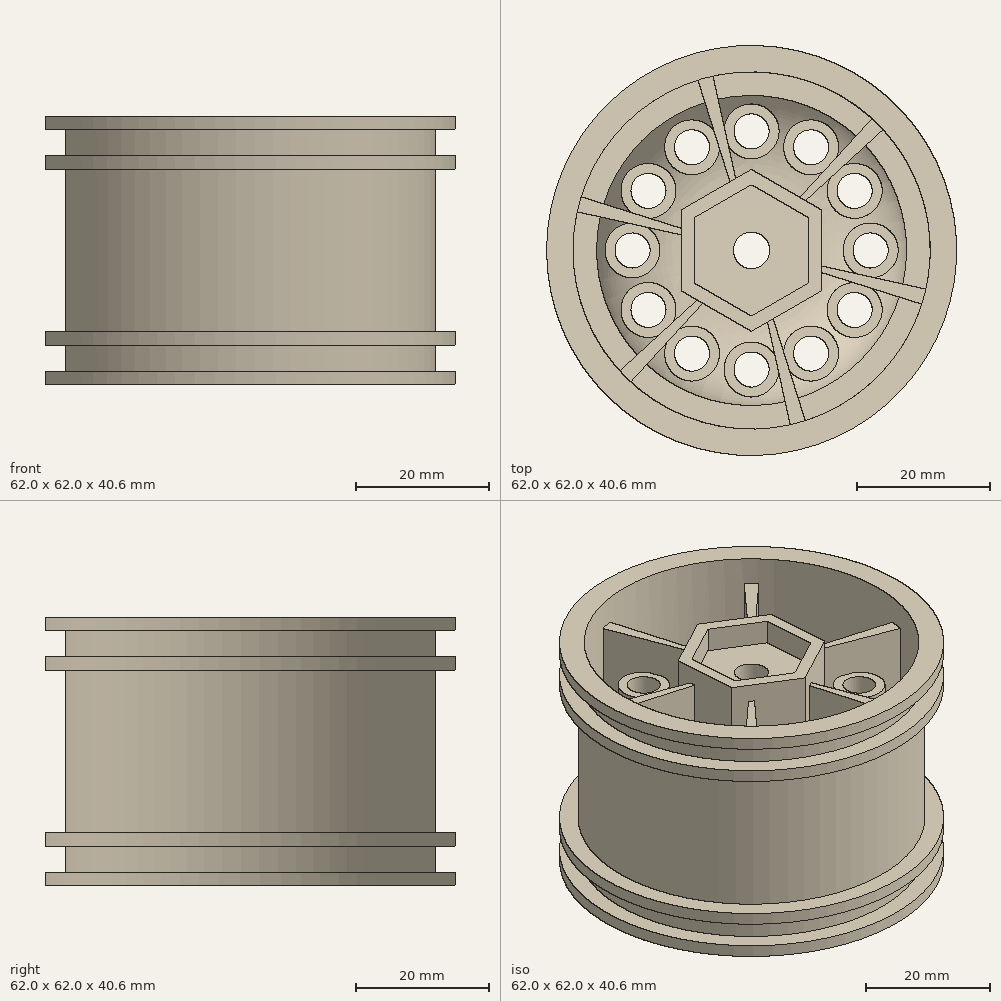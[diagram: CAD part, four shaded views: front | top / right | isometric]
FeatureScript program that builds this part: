
annotation { "Feature Type Name" : "Feature", "Feature Type Description" : "" }
export const myFeature = defineFeature(function(context is Context, id is Id, definition is map)
    precondition{}
    {
        {
            var Q0;
            Q0=qCreatedBy(makeId("Front.planeOp"),FACE);
            var sketch = newSketch(context, id + "F0", { "sketchPlane" : qUnion([Q0])});
            skLineSegment(sketch, "E0", {"start": v(31, 40.6) * mm, "end": v(0, 40.6) * mm, "construction": true});
            skLineSegment(sketch, "E1", {"start": v(0, 0) * mm, "end": v(0, 40.6) * mm});
            skPoint(sketch, "E2", {"position": v(0, 20.3) * mm});
            skLineSegment(sketch, "E3", {"start": v(31, 0) * mm, "end": v(31, 2) * mm});
            skLineSegment(sketch, "E4", {"start": v(31, 2) * mm, "end": v(28, 2) * mm});
            skLineSegment(sketch, "E5", {"start": v(28, 2) * mm, "end": v(28, 6) * mm});
            skLineSegment(sketch, "E6", {"start": v(28, 6) * mm, "end": v(31, 6) * mm});
            skLineSegment(sketch, "E7", {"start": v(31, 6) * mm, "end": v(31, 8) * mm});
            skLineSegment(sketch, "E8", {"start": v(31, 8) * mm, "end": v(28, 8) * mm});
            skLineSegment(sketch, "E9", {"start": v(28, 8) * mm, "end": v(28, 20.3) * mm});
            skLineSegment(sketch, "E10", {"start": v(31, 0) * mm, "end": v(27, 0) * mm});
            skLineSegment(sketch, "E11", {"start": v(0, 20.3) * mm, "end": v(28, 20.3) * mm, "construction": true});
            skLineSegment(sketch, "E12.MirrorCS", {"start": v(28, 32.6) * mm, "end": v(28, 20.3) * mm});
            skLineSegment(sketch, "E13.MirrorCS", {"start": v(31, 32.6) * mm, "end": v(28, 32.6) * mm});
            skLineSegment(sketch, "E14.MirrorCS", {"start": v(31, 34.6) * mm, "end": v(31, 32.6) * mm});
            skLineSegment(sketch, "E15.MirrorCS", {"start": v(28, 34.6) * mm, "end": v(31, 34.6) * mm});
            skLineSegment(sketch, "E16.MirrorCS", {"start": v(28, 38.6) * mm, "end": v(28, 34.6) * mm});
            skLineSegment(sketch, "E17.MirrorCS", {"start": v(31, 38.6) * mm, "end": v(28, 38.6) * mm});
            skLineSegment(sketch, "E18.MirrorCS", {"start": v(31, 40.6) * mm, "end": v(31, 38.6) * mm});
            skLineSegment(sketch, "E19", {"start": v(0, 20.3) * mm, "end": v(0, 24) * mm});
            skLineSegment(sketch, "E20.MirrorCS", {"start": v(31, 40.6) * mm, "end": v(27, 40.6) * mm});
            skLineSegment(sketch, "E21", {"start": v(27, 0) * mm, "end": v(27, 12) * mm});
            skLineSegment(sketch, "E22", {"start": v(27, 12) * mm, "end": v(22.5, 12) * mm});
            skLineSegment(sketch, "E23", {"start": v(0, 20.3) * mm, "end": v(10, 20.3) * mm});
            skArc(sketch, "E24", {"start": v(22.5, 12) * mm, "mid": v(18.66, 20.51) * mm, "end": v(10, 24) * mm});
            skLineSegment(sketch, "E25", {"start": v(10, 24) * mm, "end": v(0, 24) * mm});
            skLineSegment(sketch, "E26.0", {"start": v(10, 25) * mm, "end": v(0, 25) * mm});
            skArc(sketch, "E26.1", {"start": v(23.43, 13) * mm, "mid": v(19, 21.56) * mm, "end": v(10, 25) * mm});
            skLineSegment(sketch, "E26.2", {"start": v(27, 13) * mm, "end": v(23.43, 13) * mm});
            skLineSegment(sketch, "E27", {"start": v(27, 40.6) * mm, "end": v(27, 13) * mm});
            skSolve(sketch);
        }
        {
            var Q0;
            Q0=makeQuery(id+"F0.imprint","IMPRINT",FACE,{"disambiguationData":[TD([[makeQuery(id+"F0.imprint","IMPRINT",EDGE,{"derivedFrom":sQuery(id+"F0.wireOp",EDGE,"E3")}),1.0]])]});
            var Q1;
            Q1=sQuery(id+"F0.wireOp",EDGE,"E1");
            revolve(context, id + "F1", {"entities" : qUnion([Q0]), "axis" : qUnion([Q1]), "revolveType" : RevolveType.FULL});
        }
        {
            var Q0;
            Q0=makeQuery(id+"F1.opRevolve","SWEPT_FACE",FACE,{"disambiguationData":[OSD([sQuery(id+"F0.wireOp",EDGE,"E26.0")])]});
            cPlane(context, id + "F2", {"entities" : qUnion([Q0]), "cplaneType" : CPlaneType.OFFSET, "offset" : 5 * mm, "width" : 150 * mm, "height" : 150 * mm});
        }
        {
            var Q0;
            Q0=qCreatedBy(id+"F2.planeOp",FACE);
            var sketch = newSketch(context, id + "F17", { "sketchPlane" : qUnion([Q0])});
            skCircle(sketch, "E28", {"center": v(18, 0) * mm, "radius": 2.65 * mm});
            skCircle(sketch, "E29.0", {"center": v(18, 0) * mm, "radius": 4.15 * mm});
            skSolve(sketch);
        }
        {
            var Q0;
            Q0=makeQuery(id+"F17.imprint","IMPRINT",FACE,{"disambiguationData":[TD([[makeQuery(id+"F17.imprint","IMPRINT",EDGE,{"derivedFrom":sQuery(id+"F17.wireOp",EDGE,"E28")}),1.0]])]});
            extrude(context, id + "F18", {"entities" : qUnion([Q0]), "endBound" : BoundingType.THROUGH_ALL, "oppositeDirection" : true, "depth" : 25 * mm});
        }
        {
            var Q0;
            Q0=makeQuery(id+"F17.imprint","IMPRINT",FACE,{"disambiguationData":[TD([[makeQuery(id+"F17.imprint","IMPRINT",EDGE,{"derivedFrom":sQuery(id+"F17.wireOp",EDGE,"E28")}),-1.0]])]});
            extrude(context, id + "F3", {"entities" : qUnion([Q0]), "endBound" : BoundingType.UP_TO_NEXT, "oppositeDirection" : true, "depth" : 25 * mm});
        }
        {
            var Q0;
            Q0=makeQuery(id+"F18.opExtrude","SWEPT_BODY",BODY,{"disambiguationData":[OSD([sQuery(id+"F17.wireOp",EDGE,"E28")])]});
            var Q1;
            Q1=sQuery(id+"F0.wireOp",EDGE,"E1");
            circularPattern(context, id + "F19", {"operationType" : NewBodyOperationType.REMOVE, "entities" : qUnion([Q0]), "axis" : qUnion([Q1]), "angle" : 360 * degree, "instanceCount" : 12, "oppositeDirection" : true, "equalSpace" : true});
        }
        {
            var Q0;
            Q0=makeQuery(id+"F3.opExtrude","SWEPT_BODY",BODY,{"disambiguationData":[OSD([sQuery(id+"F17.wireOp",EDGE,"E28"),sQuery(id+"F17.wireOp",EDGE,"E29.0")])]});
            var Q1;
            Q1=sQuery(id+"F0.wireOp",EDGE,"E1");
            circularPattern(context, id + "F4", {"operationType" : NewBodyOperationType.ADD, "entities" : qUnion([Q0]), "axis" : qUnion([Q1]), "angle" : 360 * degree, "instanceCount" : 12, "equalSpace" : true});
        }
        {
            var Q0;
            Q0=makeQuery(id+"F1.opRevolve","SWEPT_FACE",FACE,{"disambiguationData":[OSD([sQuery(id+"F0.wireOp",EDGE,"E26.0")])]});
            cPlane(context, id + "F5", {"entities" : qUnion([Q0]), "cplaneType" : CPlaneType.OFFSET, "offset" : 10 * mm, "width" : 150 * mm, "height" : 150 * mm});
        }
        {
            var Q0;
            Q0=qCreatedBy(id+"F5.planeOp",FACE);
            var sketch = newSketch(context, id + "F20", { "sketchPlane" : qUnion([Q0])});
            skCircle(sketch, "E30", {"center": v(0, 0) * mm, "radius": 2.75 * mm});
            skCircle(sketch, "E31.cCircle", {"center": v(0, 0) * mm, "radius": 8.6 * mm, "construction": true});
            skLineSegment(sketch, "E31.0", {"start": v(-8.6, 4.97) * mm, "end": v(0, 9.93) * mm});
            skLineSegment(sketch, "E31.1", {"start": v(0, 9.93) * mm, "end": v(8.6, 4.97) * mm});
            skLineSegment(sketch, "E31.2", {"start": v(8.6, 4.97) * mm, "end": v(8.6, -4.97) * mm});
            skLineSegment(sketch, "E31.3", {"start": v(8.6, -4.97) * mm, "end": v(0, -9.93) * mm});
            skLineSegment(sketch, "E31.4", {"start": v(0, -9.93) * mm, "end": v(-8.6, -4.97) * mm});
            skLineSegment(sketch, "E31.5", {"start": v(-8.6, -4.97) * mm, "end": v(-8.6, 4.97) * mm});
            skPoint(sketch, "E31.0.midPoint", {"position": v(-4.3, 7.45) * mm});
            skLineSegment(sketch, "E32.0", {"start": v(10.6, 6.12) * mm, "end": v(10.6, -6.12) * mm});
            skLineSegment(sketch, "E32.1", {"start": v(0, -12.24) * mm, "end": v(-10.6, -6.12) * mm});
            skLineSegment(sketch, "E32.2", {"start": v(-10.6, -6.12) * mm, "end": v(-10.6, 6.12) * mm});
            skLineSegment(sketch, "E32.3", {"start": v(10.6, -6.12) * mm, "end": v(0, -12.24) * mm});
            skLineSegment(sketch, "E32.4", {"start": v(-10.6, 6.12) * mm, "end": v(0, 12.24) * mm});
            skLineSegment(sketch, "E32.5", {"start": v(0, 12.24) * mm, "end": v(10.6, 6.12) * mm});
            skCircle(sketch, "E33", {"center": v(0, 0) * mm, "radius": 6 * mm});
            skSolve(sketch);
        }
        {
            var Q0;
            Q0=makeQuery(id+"F20.imprint","IMPRINT",FACE,{"disambiguationData":[TD([[makeQuery(id+"F20.imprint","IMPRINT",EDGE,{"derivedFrom":sQuery(id+"F20.wireOp",EDGE,"E31.0")}),1.0]])]});
            var Q1;
            Q1=makeQuery(id+"F20.imprint","IMPRINT",FACE,{"disambiguationData":[TD([[makeQuery(id+"F20.imprint","IMPRINT",EDGE,{"derivedFrom":sQuery(id+"F20.wireOp",EDGE,"E30")}),-1.0]])]});
            var Q2;
            Q2=makeQuery(id+"F20.imprint","IMPRINT",FACE,{"disambiguationData":[TD([[makeQuery(id+"F20.imprint","IMPRINT",EDGE,{"derivedFrom":sQuery(id+"F20.wireOp",EDGE,"E30")}),1.0]])]});
            var Q3;
            Q3=makeQuery(id+"F20.imprint","IMPRINT",FACE,{"disambiguationData":[TD([[makeQuery(id+"F20.imprint","IMPRINT",EDGE,{"derivedFrom":sQuery(id+"F20.wireOp",EDGE,"E31.0")}),-1.0]])]});
            extrude(context, id + "F6", {"entities" : qUnion([Q0, Q1, Q2, Q3]), "operationType" : NewBodyOperationType.ADD, "endBound" : BoundingType.UP_TO_NEXT, "oppositeDirection" : true, "depth" : 20 * mm});
        }
        {
            var Q0;
            Q0=makeQuery(id+"F20.imprint","IMPRINT",FACE,{"disambiguationData":[TD([[makeQuery(id+"F20.imprint","IMPRINT",EDGE,{"derivedFrom":sQuery(id+"F20.wireOp",EDGE,"E31.0")}),1.0]])]});
            extrude(context, id + "F7", {"entities" : qUnion([Q0]), "operationType" : NewBodyOperationType.ADD, "depth" : 4 * mm});
        }
        {
            var Q0;
            Q0=makeQuery(id+"F20.imprint","IMPRINT",FACE,{"disambiguationData":[TD([[makeQuery(id+"F20.imprint","IMPRINT",EDGE,{"derivedFrom":sQuery(id+"F20.wireOp",EDGE,"E30")}),-1.0]])]});
            var Q1;
            Q1=makeQuery(id+"F20.imprint","IMPRINT",FACE,{"disambiguationData":[TD([[makeQuery(id+"F20.imprint","IMPRINT",EDGE,{"derivedFrom":sQuery(id+"F20.wireOp",EDGE,"E30")}),1.0]])]});
            extrude(context, id + "F8", {"entities" : qUnion([Q0, Q1]), "operationType" : NewBodyOperationType.REMOVE, "oppositeDirection" : true, "depth" : 25 * mm});
        }
        {
            var Q0;
            Q0=makeQuery(id+"F20.imprint","IMPRINT",FACE,{"disambiguationData":[TD([[makeQuery(id+"F20.imprint","IMPRINT",EDGE,{"derivedFrom":sQuery(id+"F20.wireOp",EDGE,"E30")}),-1.0]])]});
            extrude(context, id + "F21", {"entities" : qUnion([Q0]), "operationType" : NewBodyOperationType.ADD, "oppositeDirection" : true, "depth" : 5.5 * mm});
        }
        {
            var Q0;
            Q0=makeQuery(id+"F1.opRevolve","SWEPT_FACE",FACE,{"disambiguationData":[OSD([sQuery(id+"F0.wireOp",EDGE,"E20.MirrorCS")])]});
            var sketch = newSketch(context, id + "F22", { "sketchPlane" : qUnion([Q0])});
            skCircle(sketch, "E34.0", {"center": v(9, -15.59) * mm, "radius": 4.15 * mm});
            skCircle(sketch, "E35.0", {"center": v(0, 0) * mm, "radius": 27 * mm});
            skLineSegment(sketch, "E36", {"start": v(0, 0) * mm, "end": v(6.99, -26.08) * mm});
            skLineSegment(sketch, "E37", {"start": v(5, -16.66) * mm, "end": v(4, -16.93) * mm});
            skCircle(sketch, "E38.0", {"center": v(0, -18) * mm, "radius": 4.15 * mm});
            skPoint(sketch, "E39", {"position": v(4.5, -16.8) * mm});
            skLineSegment(sketch, "E40", {"start": v(16.26, -23.6) * mm, "end": v(-9.38, -30.46) * mm});
            skSolve(sketch);
        }
        {
            var Q0;
            Q0=sQuery(id+"F22.wireOp",EDGE,"E36");
            var Q1;
            Q1=qCreatedBy(makeId("Origin.pointOp"),VERTEX);
            cPlane(context, id + "F9", {"entities" : qUnion([Q0, Q1]), "cplaneType" : CPlaneType.LINE_ANGLE, "offset" : 25 * mm, "angle" : 0 * degree, "width" : 150 * mm, "height" : 150 * mm});
        }
        {
            var Q0;
            Q0=qCreatedBy(id+"F9.planeOp",FACE);
            var sketch = newSketch(context, id + "F10", { "sketchPlane" : qUnion([Q0])});
            skLineSegment(sketch, "E41", {"start": v(31, 40.6) * mm, "end": v(0, 40.6) * mm, "construction": true});
            skLineSegment(sketch, "E42", {"start": v(0, 0) * mm, "end": v(0, 40.6) * mm});
            skPoint(sketch, "E43", {"position": v(0, 20.3) * mm});
            skLineSegment(sketch, "E44", {"start": v(31, 0) * mm, "end": v(31, 2) * mm});
            skLineSegment(sketch, "E45", {"start": v(31, 2) * mm, "end": v(28, 2) * mm});
            skLineSegment(sketch, "E46", {"start": v(28, 2) * mm, "end": v(28, 6) * mm});
            skLineSegment(sketch, "E47", {"start": v(28, 6) * mm, "end": v(31, 6) * mm});
            skLineSegment(sketch, "E48", {"start": v(31, 6) * mm, "end": v(31, 8) * mm});
            skLineSegment(sketch, "E49", {"start": v(31, 8) * mm, "end": v(28, 8) * mm});
            skLineSegment(sketch, "E50", {"start": v(28, 8) * mm, "end": v(28, 20.3) * mm});
            skLineSegment(sketch, "E51", {"start": v(31, 0) * mm, "end": v(27, 0) * mm});
            skLineSegment(sketch, "E52", {"start": v(0, 20.3) * mm, "end": v(28, 20.3) * mm, "construction": true});
            skLineSegment(sketch, "E53.MirrorCS", {"start": v(28, 32.6) * mm, "end": v(28, 20.3) * mm});
            skLineSegment(sketch, "E54.MirrorCS", {"start": v(31, 32.6) * mm, "end": v(28, 32.6) * mm});
            skLineSegment(sketch, "E55.MirrorCS", {"start": v(31, 34.6) * mm, "end": v(31, 32.6) * mm});
            skLineSegment(sketch, "E56.MirrorCS", {"start": v(28, 34.6) * mm, "end": v(31, 34.6) * mm});
            skLineSegment(sketch, "E57.MirrorCS", {"start": v(28, 38.6) * mm, "end": v(28, 34.6) * mm});
            skLineSegment(sketch, "E58.MirrorCS", {"start": v(31, 38.6) * mm, "end": v(28, 38.6) * mm});
            skLineSegment(sketch, "E59.MirrorCS", {"start": v(31, 40.6) * mm, "end": v(31, 38.6) * mm});
            skLineSegment(sketch, "E60", {"start": v(0, 20.3) * mm, "end": v(0, 24) * mm});
            skLineSegment(sketch, "E61.MirrorCS", {"start": v(31, 40.6) * mm, "end": v(27, 40.6) * mm});
            skLineSegment(sketch, "E62", {"start": v(27, 0) * mm, "end": v(27, 12) * mm});
            skLineSegment(sketch, "E63", {"start": v(27, 12) * mm, "end": v(22.5, 12) * mm});
            skLineSegment(sketch, "E64", {"start": v(0, 20.3) * mm, "end": v(10, 20.3) * mm});
            skArc(sketch, "E65", {"start": v(22.5, 12) * mm, "mid": v(18.66, 20.51) * mm, "end": v(10, 24) * mm});
            skLineSegment(sketch, "E66", {"start": v(10, 24) * mm, "end": v(0, 24) * mm});
            skLineSegment(sketch, "E67.0", {"start": v(10, 25) * mm, "end": v(0, 25) * mm});
            skArc(sketch, "E67.1", {"start": v(23.43, 13) * mm, "mid": v(19, 21.56) * mm, "end": v(10, 25) * mm});
            skLineSegment(sketch, "E67.2", {"start": v(27, 13) * mm, "end": v(23.43, 13) * mm});
            skLineSegment(sketch, "E68", {"start": v(27, 40.6) * mm, "end": v(27, 13) * mm});
            skLineSegment(sketch, "E69.0.0", {"start": v(-8.65, 39) * mm, "end": v(3.17, 39) * mm});
            skLineSegment(sketch, "E69.0.1", {"start": v(3.17, 39) * mm, "end": v(11.82, 39) * mm});
            skLineSegment(sketch, "E69.0.2", {"start": v(11.82, 39) * mm, "end": v(8.65, 39) * mm});
            skLineSegment(sketch, "E69.0.3", {"start": v(8.65, 39) * mm, "end": v(-3.17, 39) * mm});
            skLineSegment(sketch, "E69.0.4", {"start": v(-3.17, 39) * mm, "end": v(-11.82, 39) * mm});
            skLineSegment(sketch, "E69.0.5", {"start": v(-11.82, 39) * mm, "end": v(-8.65, 39) * mm});
            skLineSegment(sketch, "E70.0.0", {"start": v(3.17, 39) * mm, "end": v(3.17, 24.81) * mm});
            skFitSpline(sketch, "E70.0.1", {"points": [v(3.14, 24.83) * mm, v(3.85, 24.91) * mm, v(5.28, 24.98) * mm, v(7.42, 25) * mm, v(9.57, 24.98) * mm, v(11, 24.91) * mm, v(11.71, 24.83) * mm]});
            skLineSegment(sketch, "E70.0.2", {"start": v(11.82, 24.81) * mm, "end": v(11.82, 39) * mm});
            skLineSegment(sketch, "E70.0.3", {"start": v(11.82, 39) * mm, "end": v(3.17, 39) * mm});
            skLineSegment(sketch, "E71.0.0", {"start": v(7.02, 35) * mm, "end": v(9.6, 35) * mm});
            skLineSegment(sketch, "E71.0.1", {"start": v(9.6, 35) * mm, "end": v(9.6, 39) * mm});
            skLineSegment(sketch, "E71.0.2", {"start": v(9.6, 39) * mm, "end": v(7.02, 39) * mm});
            skLineSegment(sketch, "E71.0.3", {"start": v(7.02, 39) * mm, "end": v(7.02, 35) * mm});
            skLineSegment(sketch, "E72", {"start": v(11.82, 36) * mm, "end": v(27, 36) * mm});
            skLineSegment(sketch, "E73", {"start": v(11.82, 36) * mm, "end": v(10.82, 36) * mm});
            skLineSegment(sketch, "E74", {"start": v(10.82, 36) * mm, "end": v(10.82, 24.97) * mm});
            skSolve(sketch);
        }
        {
            var Q0;
            {var subQ5=sQuery(id+"F10.wireOp",EDGE,"E67.2");Q0=makeQuery(id+"F10.imprint","IMPRINT",FACE,{"disambiguationData":[TD([[makeQuery(id+"F10.imprint","IMPRINT",EDGE,{"derivedFrom":subQ5}),-1.0]])]});}
            var Q1;
            {var subQ4=sQuery(id+"F10.wireOp",EDGE,"E73");Q1=makeQuery(id+"F10.imprint","IMPRINT",FACE,{"disambiguationData":[TD([[makeQuery(id+"F10.imprint","IMPRINT",EDGE,{"derivedFrom":subQ4}),1.0]])]});}
            var Q2;
            Q2=sQuery(id+"F0.wireOp",EDGE,"E1");
            revolve(context, id + "F11", {"entities" : qUnion([Q0, Q1]), "axis" : qUnion([Q2]), "revolveType" : RevolveType.SYMMETRIC, "angle" : 5 * degree});
        }
        {
            var Q0;
            Q0=makeQuery(id+"F11.opRevolve","SWEPT_BODY",BODY,{"disambiguationData":[OSD([sQuery(id+"F10.wireOp",EDGE,"E67.1"),sQuery(id+"F10.wireOp",EDGE,"E67.2"),sQuery(id+"F10.wireOp",EDGE,"E68"),sQuery(id+"F10.wireOp",EDGE,"E72"),sQuery(id+"F10.wireOp",EDGE,"E73"),sQuery(id+"F10.wireOp",EDGE,"E74")])]});
            var Q1;
            Q1=sQuery(id+"F0.wireOp",EDGE,"E1");
            circularPattern(context, id + "F12", {"operationType" : NewBodyOperationType.ADD, "entities" : qUnion([Q0]), "axis" : qUnion([Q1]), "angle" : 360 * degree, "instanceCount" : 6, "equalSpace" : true});
        }
        {
            var Q0;
            Q0=makeQuery(id+"F1.opRevolve","SWEPT_FACE",FACE,{"disambiguationData":[OSD([sQuery(id+"F0.wireOp",EDGE,"E25")])]});
            var sketch = newSketch(context, id + "F13", { "sketchPlane" : qUnion([Q0])});
            skArc(sketch, "E75", {"start": v(-8, 0) * mm, "mid": v(-9, 1) * mm, "end": v(-10, 0) * mm});
            skLineSegment(sketch, "E76", {"start": v(-0.63, 0) * mm, "end": v(-14.19, 0) * mm, "construction": true});
            skLineSegment(sketch, "E77", {"start": v(-10, 0) * mm, "end": v(-8, 0) * mm});
            skSolve(sketch);
        }
        {
            var Q0;
            Q0=makeQuery(id+"F13.imprint","IMPRINT",FACE,{"disambiguationData":[TD([[makeQuery(id+"F13.imprint","IMPRINT",EDGE,{"derivedFrom":sQuery(id+"F13.wireOp",EDGE,"E75")}),1.0]])]});
            var Q1;
            Q1=sQuery(id+"F13.wireOp",EDGE,"E77");
            revolve(context, id + "F23", {"entities" : qUnion([Q0]), "axis" : qUnion([Q1]), "revolveType" : RevolveType.FULL});
        }
        {
            var Q0;
            Q0=makeQuery(id+"F23.opRevolve","SWEPT_BODY",BODY,{"disambiguationData":[OSD([sQuery(id+"F13.wireOp",EDGE,"E75"),sQuery(id+"F13.wireOp",EDGE,"E77")])]});
            var Q1;
            Q1=qCreatedBy(makeId("Origin.pointOp"),BODY);
            var Q2;
            Q2=makeQuery(id+"F8.boolean.opBoolean","INTERSECT",EDGE,{"derivedFrom":[makeQuery(id+"F1.opRevolve","SWEPT_FACE",FACE,{"disambiguationData":[OSD([sQuery(id+"F0.wireOp",EDGE,"E25")])]}),makeQuery(id+"F8.opExtrude","SWEPT_FACE",FACE,{"disambiguationData":[OSD([sQuery(id+"F20.wireOp",EDGE,"E33")])]})]});
            circularPattern(context, id + "F24", {"operationType" : NewBodyOperationType.ADD, "entities" : qUnion([Q0, Q1]), "axis" : qUnion([Q2]), "angle" : 360 * degree, "instanceCount" : 5, "equalSpace" : true});
        }
        {
            var Q0;
            Q0=makeQuery(id+"F1.opRevolve","SWEPT_FACE",FACE,{"disambiguationData":[OSD([sQuery(id+"F0.wireOp",EDGE,"E22")])]});
            var sketch = newSketch(context, id + "F14", { "sketchPlane" : qUnion([Q0])});
            skArc(sketch, "E78", {"start": v(-24, 0) * mm, "mid": v(-25, 1) * mm, "end": v(-26, 0) * mm});
            skLineSegment(sketch, "E79", {"start": v(-26, 0) * mm, "end": v(-24, 0) * mm});
            skSolve(sketch);
        }
        {
            var Q0;
            Q0=makeQuery(id+"F14.imprint","IMPRINT",FACE,{"disambiguationData":[TD([[makeQuery(id+"F14.imprint","IMPRINT",EDGE,{"derivedFrom":sQuery(id+"F14.wireOp",EDGE,"E78")}),1.0]])]});
            var Q1;
            Q1=sQuery(id+"F14.wireOp",EDGE,"E79");
            revolve(context, id + "F15", {"entities" : qUnion([Q0]), "axis" : qUnion([Q1]), "revolveType" : RevolveType.FULL});
        }
        {
            var Q0;
            Q0=makeQuery(id+"F15.opRevolve","SWEPT_BODY",BODY,{"disambiguationData":[OSD([sQuery(id+"F14.wireOp",EDGE,"E78"),sQuery(id+"F14.wireOp",EDGE,"E79")])]});
            var Q1;
            Q1=makeQuery(id+"F1.opRevolve","SWEPT_EDGE",EDGE,{"disambiguationData":[OSD([sQuery(id+"F0.wireOp",EDGE,"E10"),sQuery(id+"F0.wireOp",EDGE,"E21")])]});
            circularPattern(context, id + "F16", {"operationType" : NewBodyOperationType.ADD, "entities" : qUnion([Q0]), "axis" : qUnion([Q1]), "angle" : 360 * degree, "instanceCount" : 30, "equalSpace" : true});
        }
    });
